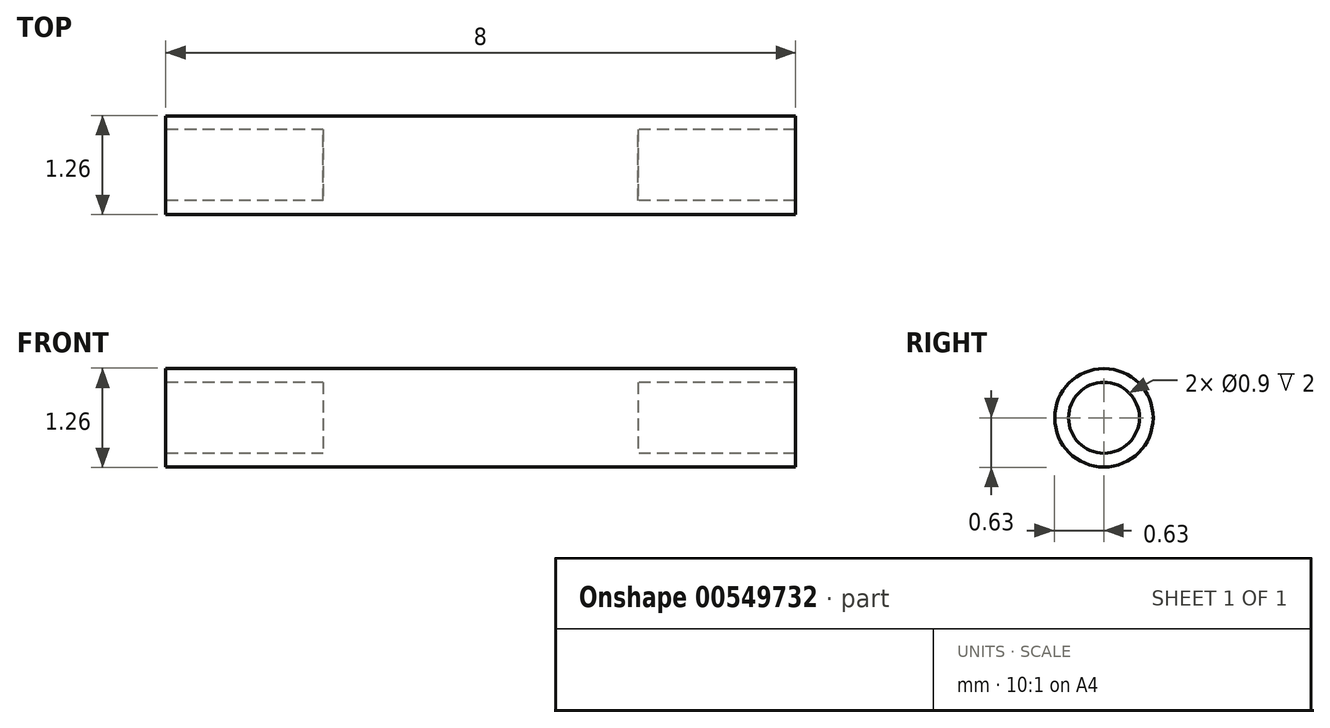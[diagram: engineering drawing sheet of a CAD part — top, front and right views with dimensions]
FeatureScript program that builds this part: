
annotation { "Feature Type Name" : "Feature", "Feature Type Description" : "" }
export const myFeature = defineFeature(function(context is Context, id is Id, definition is map)
    precondition{}
    {
        {
            var Q0;
            Q0=qCreatedBy(makeId("Front.planeOp"),FACE);
            var sketch = newSketch(context, id + "F0", { "sketchPlane" : qUnion([Q0])});
            skLineSegment(sketch, "E0", {"start": v(-82.57, 0) * mm, "end": v(90.42, 0) * mm});
            skLineSegment(sketch, "E1", {"start": v(0, 0.63) * mm, "end": v(4, 0.63) * mm});
            skLineSegment(sketch, "E2.0", {"start": v(4, 0.63) * mm, "end": v(4, 0.45) * mm});
            skLineSegment(sketch, "E3.0", {"start": v(2, 0.45) * mm, "end": v(2, 0) * mm});
            skLineSegment(sketch, "E4.0", {"start": v(2, 0.45) * mm, "end": v(4, 0.45) * mm});
            skPoint(sketch, "E5.orphan", {"position": v(0, 30.3) * mm});
            skPoint(sketch, "E6.orphan", {"position": v(-57.08, 0.63) * mm});
            skLineSegment(sketch, "E7.MirrorCS", {"start": v(-2, 0.45) * mm, "end": v(-4, 0.45) * mm});
            skLineSegment(sketch, "E8.MirrorCS", {"start": v(0, 0.63) * mm, "end": v(-4, 0.63) * mm});
            skLineSegment(sketch, "E9.MirrorCS", {"start": v(-2, 0.45) * mm, "end": v(-2, 0) * mm});
            skLineSegment(sketch, "E10.MirrorCS", {"start": v(-4, 0.63) * mm, "end": v(-4, 0.45) * mm});
            skPoint(sketch, "E11.orphan", {"position": v(0, 0.45) * mm});
            skPoint(sketch, "E12.orphan", {"position": v(-2, 0.63) * mm});
            skPoint(sketch, "E13.orphan", {"position": v(2, 0.63) * mm});
            skSolve(sketch);
        }
        {
            var Q0;
            Q0 = qSketchRegion(id + "F0", true);
            var Q1;
            Q1=sQuery(id+"F0.wireOp",EDGE,"E0");
            revolve(context, id + "F1", {"entities" : qUnion([Q0]), "axis" : qUnion([Q1]), "revolveType" : RevolveType.FULL});
        }
    });
